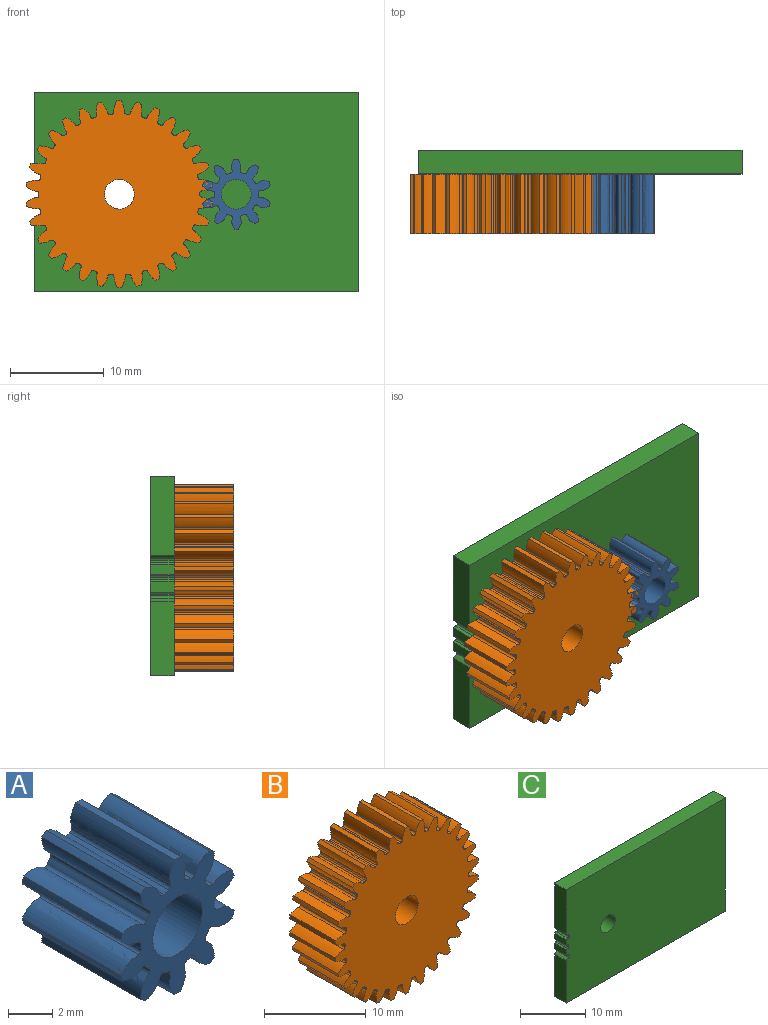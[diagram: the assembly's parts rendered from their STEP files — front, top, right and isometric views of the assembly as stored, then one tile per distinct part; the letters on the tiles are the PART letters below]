
ASSEMBLY  parts=3 mates=2
PART A: 63 faces, bbox 7.3x6.4x7.5 mm
  f0: cylinder r=3.75mm len=6.35mm, axis (0,1,0), area 2.3mm2, adj f9,f12,f53,f60
  f1: cylinder r=3.75mm len=6.35mm, axis (0,1,0), area 2.3mm2, adj f9,f12,f13,f55
  f2: cylinder r=3.75mm len=6.35mm, axis (0,1,0), area 2.3mm2, adj f9,f12,f43,f50
  f3: cylinder r=3.75mm len=6.35mm, axis (0,1,0), area 2.3mm2, adj f9,f12,f45,f58
  f4: cylinder r=3.75mm len=6.35mm, axis (0,1,0), area 2.3mm2, adj f9,f12,f33,f40
  f5: cylinder r=3.75mm len=6.35mm, axis (0,1,0), area 2.3mm2, adj f9,f12,f28,f35
  f6: cylinder r=3.75mm len=6.35mm, axis (0,1,0), area 2.3mm2, adj f9,f12,f23,f30
  f7: cylinder r=3.75mm len=6.35mm, axis (0,1,0), area 2.3mm2, adj f9,f12,f25,f48
  f8: cylinder r=3.75mm len=6.35mm, axis (0,1,0), area 2.3mm2, adj f9,f12,f20,f38
  f9: plane 7.51x7.25mm, normal (0,-1,0), area 21.3mm2, adj f0,f1,f2,f3,f4,f5,f6,f7
  f10: cylinder r=1.59mm len=6.35mm, axis (0,1,0), area 63.3mm2, adj f9,f12
  f11: cylinder r=3.75mm len=6.35mm, axis (0,1,0), area 2.3mm2, adj f9,f12,f15,f18
  f12: plane 7.51x7.25mm, normal (0,1,0), area 21.3mm2, adj f0,f1,f2,f3,f4,f5,f6,f7
  f13: extruded ~6.35x1.11mm, area 8.4mm2, adj f1,f9,f12,f16
  f14: cylinder r=2.34mm len=6.35mm, axis (0,1,0), area 2mm2, adj f9,f12,f16,f17
  f15: extruded ~6.35x1.11mm, area 8.4mm2, adj f9,f11,f12,f17
  f16: cylinder r=0.19mm len=6.35mm, axis (0,1,0), area 1.8mm2, adj f9,f12,f13,f14
  f17: cylinder r=0.19mm len=6.35mm, axis (0,1,0), area 1.8mm2, adj f9,f12,f14,f15
  f18: extruded ~6.35x1.27mm, area 8.4mm2, adj f9,f11,f12,f21
  f19: cylinder r=2.34mm len=6.35mm, axis (0,1,0), area 2mm2, adj f9,f12,f21,f22
  f20: extruded ~6.35x1.16mm, area 8.4mm2, adj f8,f9,f12,f22
  f21: cylinder r=0.19mm len=6.35mm, axis (0,1,0), area 1.8mm2, adj f9,f12,f18,f19
  f22: cylinder r=0.19mm len=6.35mm, axis (0,1,0), area 1.8mm2, adj f9,f12,f19,f20
  f23: extruded ~6.35x1.11mm, area 8.4mm2, adj f6,f9,f12,f26
  f24: cylinder r=2.34mm len=6.35mm, axis (0,1,0), area 2mm2, adj f9,f12,f26,f27
  f25: extruded ~6.35x1.11mm, area 8.4mm2, adj f7,f9,f12,f27
  f26: cylinder r=0.19mm len=6.35mm, axis (0,1,0), area 1.8mm2, adj f9,f12,f23,f24
  f27: cylinder r=0.19mm len=6.35mm, axis (0,1,0), area 1.8mm2, adj f9,f12,f24,f25
  f28: extruded ~6.35x1.16mm, area 8.4mm2, adj f5,f9,f12,f31
  f29: cylinder r=2.34mm len=6.35mm, axis (0,1,0), area 2mm2, adj f9,f12,f31,f32
  f30: extruded ~6.35x1.27mm, area 8.4mm2, adj f6,f9,f12,f32
  f31: cylinder r=0.19mm len=6.35mm, axis (0,1,0), area 1.8mm2, adj f9,f12,f28,f29
  f32: cylinder r=0.19mm len=6.35mm, axis (0,1,0), area 1.8mm2, adj f9,f12,f29,f30
  f33: extruded ~6.35x1.25mm, area 8.4mm2, adj f4,f9,f12,f36
  f34: cylinder r=2.34mm len=6.35mm, axis (0,1,0), area 2mm2, adj f9,f12,f36,f37
  f35: extruded ~6.35x0.94mm, area 8.4mm2, adj f5,f9,f12,f37
  f36: cylinder r=0.19mm len=6.35mm, axis (0,1,0), area 1.8mm2, adj f9,f12,f33,f34
  f37: cylinder r=0.19mm len=6.35mm, axis (0,1,0), area 1.8mm2, adj f9,f12,f34,f35
  f38: extruded ~6.35x0.94mm, area 8.4mm2, adj f8,f9,f12,f41
  f39: cylinder r=2.34mm len=6.35mm, axis (0,1,0), area 2mm2, adj f9,f12,f41,f42
  f40: extruded ~6.35x1.25mm, area 8.4mm2, adj f4,f9,f12,f42
  f41: cylinder r=0.19mm len=6.35mm, axis (0,1,0), area 1.8mm2, adj f9,f12,f38,f39
  f42: cylinder r=0.19mm len=6.35mm, axis (0,1,0), area 1.8mm2, adj f9,f12,f39,f40
  f43: extruded ~6.35x0.94mm, area 8.4mm2, adj f2,f9,f12,f46
  f44: cylinder r=2.34mm len=6.35mm, axis (0,1,0), area 2mm2, adj f9,f12,f46,f47
  f45: extruded ~6.35x1.25mm, area 8.4mm2, adj f3,f9,f12,f47
  f46: cylinder r=0.19mm len=6.35mm, axis (0,1,0), area 1.8mm2, adj f9,f12,f43,f44
  f47: cylinder r=0.19mm len=6.35mm, axis (0,1,0), area 1.8mm2, adj f9,f12,f44,f45
  f48: extruded ~6.35x1.27mm, area 8.4mm2, adj f7,f9,f12,f51
  f49: cylinder r=2.34mm len=6.35mm, axis (0,1,0), area 2mm2, adj f9,f12,f51,f52
  f50: extruded ~6.35x1.16mm, area 8.4mm2, adj f2,f9,f12,f52
  f51: cylinder r=0.19mm len=6.35mm, axis (0,1,0), area 1.8mm2, adj f9,f12,f48,f49
  f52: cylinder r=0.19mm len=6.35mm, axis (0,1,0), area 1.8mm2, adj f9,f12,f49,f50
  f53: extruded ~6.35x1.16mm, area 8.4mm2, adj f0,f9,f12,f56
  f54: cylinder r=2.34mm len=6.35mm, axis (0,1,0), area 2mm2, adj f9,f12,f56,f57
  f55: extruded ~6.35x1.27mm, area 8.4mm2, adj f1,f9,f12,f57
  f56: cylinder r=0.19mm len=6.35mm, axis (0,1,0), area 1.8mm2, adj f9,f12,f53,f54
  f57: cylinder r=0.19mm len=6.35mm, axis (0,1,0), area 1.8mm2, adj f9,f12,f54,f55
  f58: extruded ~6.35x1.25mm, area 8.4mm2, adj f3,f9,f12,f61
  f59: cylinder r=2.34mm len=6.35mm, axis (0,1,0), area 2mm2, adj f9,f12,f61,f62
  f60: extruded ~6.35x0.94mm, area 8.4mm2, adj f0,f9,f12,f62
  f61: cylinder r=0.19mm len=6.35mm, axis (0,1,0), area 1.8mm2, adj f9,f12,f58,f59
  f62: cylinder r=0.19mm len=6.35mm, axis (0,1,0), area 1.8mm2, adj f9,f12,f59,f60
PART B: 183 faces, bbox 19.9x6.4x20 mm
  f0: cylinder r=10mm len=6.35mm, axis (0,1,0), area 2.9mm2, adj f29,f32,f173,f180
  f1: cylinder r=10mm len=6.35mm, axis (0,1,0), area 2.9mm2, adj f29,f32,f168,f175
  f2: cylinder r=10mm len=6.35mm, axis (0,1,0), area 2.9mm2, adj f29,f32,f163,f170
  f3: cylinder r=10mm len=6.35mm, axis (0,1,0), area 2.9mm2, adj f29,f32,f153,f165
  f4: cylinder r=10mm len=6.35mm, axis (0,1,0), area 2.9mm2, adj f29,f32,f148,f160
  f5: cylinder r=10mm len=6.35mm, axis (0,1,0), area 2.9mm2, adj f29,f32,f155,f158
  f6: cylinder r=10mm len=6.35mm, axis (0,1,0), area 2.9mm2, adj f29,f32,f143,f150
  f7: cylinder r=10mm len=6.35mm, axis (0,1,0), area 2.9mm2, adj f29,f32,f33,f145
  f8: cylinder r=10mm len=6.35mm, axis (0,1,0), area 2.9mm2, adj f29,f32,f128,f140
  f9: cylinder r=10mm len=6.35mm, axis (0,1,0), area 2.9mm2, adj f29,f32,f135,f138
  f10: cylinder r=10mm len=6.35mm, axis (0,1,0), area 2.9mm2, adj f29,f32,f123,f130
  f11: cylinder r=10mm len=6.35mm, axis (0,1,0), area 2.9mm2, adj f29,f32,f125,f178
  f12: cylinder r=10mm len=6.35mm, axis (0,1,0), area 2.9mm2, adj f29,f32,f120,f133
  f13: cylinder r=10mm len=6.35mm, axis (0,1,0), area 2.9mm2, adj f29,f32,f115,f118
  f14: cylinder r=10mm len=6.35mm, axis (0,1,0), area 2.9mm2, adj f29,f32,f110,f113
  f15: cylinder r=10mm len=6.35mm, axis (0,1,0), area 2.9mm2, adj f29,f32,f105,f108
  f16: cylinder r=10mm len=6.35mm, axis (0,1,0), area 2.9mm2, adj f29,f32,f88,f100
  f17: cylinder r=10mm len=6.35mm, axis (0,1,0), area 2.9mm2, adj f29,f32,f95,f98
  f18: cylinder r=10mm len=6.35mm, axis (0,1,0), area 2.9mm2, adj f29,f32,f83,f90
  f19: cylinder r=10mm len=6.35mm, axis (0,1,0), area 2.9mm2, adj f29,f32,f85,f103
  f20: cylinder r=10mm len=6.35mm, axis (0,1,0), area 2.9mm2, adj f29,f32,f80,f93
  f21: cylinder r=10mm len=6.35mm, axis (0,1,0), area 2.9mm2, adj f29,f32,f75,f78
  f22: cylinder r=10mm len=6.35mm, axis (0,1,0), area 2.9mm2, adj f29,f32,f70,f73
  f23: cylinder r=10mm len=6.35mm, axis (0,1,0), area 2.9mm2, adj f29,f32,f65,f68
  f24: cylinder r=10mm len=6.35mm, axis (0,1,0), area 2.9mm2, adj f29,f32,f53,f60
  f25: cylinder r=10mm len=6.35mm, axis (0,1,0), area 2.9mm2, adj f29,f32,f43,f55
  f26: cylinder r=10mm len=6.35mm, axis (0,1,0), area 2.9mm2, adj f29,f32,f50,f63
  f27: cylinder r=10mm len=6.35mm, axis (0,1,0), area 2.9mm2, adj f29,f32,f45,f48
  f28: cylinder r=10mm len=6.35mm, axis (0,1,0), area 2.9mm2, adj f29,f32,f40,f58
  f29: plane 20x19.93mm, normal (0,-1,0), area 265.1mm2, adj f0,f1,f2,f3,f4,f5,f6,f7
  f30: cylinder r=1.59mm len=6.35mm, axis (0,1,0), area 63.3mm2, adj f29,f32
  f31: cylinder r=10mm len=6.35mm, axis (0,1,0), area 2.9mm2, adj f29,f32,f35,f38
  f32: plane 20x19.93mm, normal (0,1,0), area 265.1mm2, adj f0,f1,f2,f3,f4,f5,f6,f7
  f33: extruded ~6.35x1.16mm, area 8mm2, adj f7,f29,f32,f36
  f34: cylinder r=8.59mm len=6.35mm, axis (0,1,0), area 1.2mm2, adj f29,f32,f36,f37
  f35: extruded ~6.35x1.16mm, area 8mm2, adj f29,f31,f32,f37
  f36: cylinder r=0.23mm len=6.35mm, axis (0,1,0), area 2.2mm2, adj f29,f32,f33,f34
  f37: cylinder r=0.23mm len=6.35mm, axis (0,1,0), area 2.2mm2, adj f29,f32,f34,f35
  f38: extruded ~6.35x1.23mm, area 8mm2, adj f29,f31,f32,f41
  f39: cylinder r=8.59mm len=6.35mm, axis (0,1,0), area 1.2mm2, adj f29,f32,f41,f42
  f40: extruded ~6.35x1.03mm, area 8mm2, adj f28,f29,f32,f42
  f41: cylinder r=0.23mm len=6.35mm, axis (0,1,0), area 2.2mm2, adj f29,f32,f38,f39
  f42: cylinder r=0.23mm len=6.35mm, axis (0,1,0), area 2.2mm2, adj f29,f32,f39,f40
  f43: extruded ~6.35x1.14mm, area 8mm2, adj f25,f29,f32,f46
  f44: cylinder r=8.59mm len=6.35mm, axis (0,1,0), area 1.2mm2, adj f29,f32,f46,f47
  f45: extruded ~6.35x1.19mm, area 8mm2, adj f27,f29,f32,f47
  f46: cylinder r=0.23mm len=6.35mm, axis (0,1,0), area 2.2mm2, adj f29,f32,f43,f44
  f47: cylinder r=0.23mm len=6.35mm, axis (0,1,0), area 2.2mm2, adj f29,f32,f44,f45
  f48: extruded ~6.35x1mm, area 8mm2, adj f27,f29,f32,f51
  f49: cylinder r=8.59mm len=6.35mm, axis (0,1,0), area 1.2mm2, adj f29,f32,f51,f52
  f50: extruded ~6.35x1.25mm, area 8mm2, adj f26,f29,f32,f52
  f51: cylinder r=0.23mm len=6.35mm, axis (0,1,0), area 2.2mm2, adj f29,f32,f48,f49
  f52: cylinder r=0.23mm len=6.35mm, axis (0,1,0), area 2.2mm2, adj f29,f32,f49,f50
  f53: extruded ~6.35x1.22mm, area 8mm2, adj f24,f29,f32,f56
  f54: cylinder r=8.59mm len=6.35mm, axis (0,1,0), area 1.2mm2, adj f29,f32,f56,f57
  f55: extruded ~6.35x1.07mm, area 8mm2, adj f25,f29,f32,f57
  f56: cylinder r=0.23mm len=6.35mm, axis (0,1,0), area 2.2mm2, adj f29,f32,f53,f54
  f57: cylinder r=0.23mm len=6.35mm, axis (0,1,0), area 2.2mm2, adj f29,f32,f54,f55
  f58: extruded ~6.35x1.26mm, area 8mm2, adj f28,f29,f32,f61
  f59: cylinder r=8.59mm len=6.35mm, axis (0,1,0), area 1.2mm2, adj f29,f32,f61,f62
  f60: extruded ~6.35x0.92mm, area 8mm2, adj f24,f29,f32,f62
  f61: cylinder r=0.23mm len=6.35mm, axis (0,1,0), area 2.2mm2, adj f29,f32,f58,f59
  f62: cylinder r=0.23mm len=6.35mm, axis (0,1,0), area 2.2mm2, adj f29,f32,f59,f60
  f63: extruded ~6.35x0.95mm, area 8mm2, adj f26,f29,f32,f66
  f64: cylinder r=8.59mm len=6.35mm, axis (0,1,0), area 1.2mm2, adj f29,f32,f66,f67
  f65: extruded ~6.35x1.25mm, area 8mm2, adj f23,f29,f32,f67
  f66: cylinder r=0.23mm len=6.35mm, axis (0,1,0), area 2.2mm2, adj f29,f32,f63,f64
  f67: cylinder r=0.23mm len=6.35mm, axis (0,1,0), area 2.2mm2, adj f29,f32,f64,f65
  f68: extruded ~6.35x1.1mm, area 8mm2, adj f23,f29,f32,f71
  f69: cylinder r=8.59mm len=6.35mm, axis (0,1,0), area 1.2mm2, adj f29,f32,f71,f72
  f70: extruded ~6.35x1.2mm, area 8mm2, adj f22,f29,f32,f72
  f71: cylinder r=0.23mm len=6.35mm, axis (0,1,0), area 2.2mm2, adj f29,f32,f68,f69
  f72: cylinder r=0.23mm len=6.35mm, axis (0,1,0), area 2.2mm2, adj f29,f32,f69,f70
  f73: extruded ~6.35x1.2mm, area 8mm2, adj f22,f29,f32,f76
  f74: cylinder r=8.59mm len=6.35mm, axis (0,1,0), area 1.2mm2, adj f29,f32,f76,f77
  f75: extruded ~6.35x1.1mm, area 8mm2, adj f21,f29,f32,f77
  f76: cylinder r=0.23mm len=6.35mm, axis (0,1,0), area 2.2mm2, adj f29,f32,f73,f74
  f77: cylinder r=0.23mm len=6.35mm, axis (0,1,0), area 2.2mm2, adj f29,f32,f74,f75
  f78: extruded ~6.35x1.25mm, area 8mm2, adj f21,f29,f32,f81
  f79: cylinder r=8.59mm len=6.35mm, axis (0,1,0), area 1.2mm2, adj f29,f32,f81,f82
  f80: extruded ~6.35x0.95mm, area 8mm2, adj f20,f29,f32,f82
  f81: cylinder r=0.23mm len=6.35mm, axis (0,1,0), area 2.2mm2, adj f29,f32,f78,f79
  f82: cylinder r=0.23mm len=6.35mm, axis (0,1,0), area 2.2mm2, adj f29,f32,f79,f80
  f83: extruded ~6.35x0.92mm, area 8mm2, adj f18,f29,f32,f86
  f84: cylinder r=8.59mm len=6.35mm, axis (0,1,0), area 1.2mm2, adj f29,f32,f86,f87
  f85: extruded ~6.35x1.26mm, area 8mm2, adj f19,f29,f32,f87
  f86: cylinder r=0.23mm len=6.35mm, axis (0,1,0), area 2.2mm2, adj f29,f32,f83,f84
  f87: cylinder r=0.23mm len=6.35mm, axis (0,1,0), area 2.2mm2, adj f29,f32,f84,f85
  f88: extruded ~6.35x1.07mm, area 8mm2, adj f16,f29,f32,f91
  f89: cylinder r=8.59mm len=6.35mm, axis (0,1,0), area 1.2mm2, adj f29,f32,f91,f92
  f90: extruded ~6.35x1.22mm, area 8mm2, adj f18,f29,f32,f92
  f91: cylinder r=0.23mm len=6.35mm, axis (0,1,0), area 2.2mm2, adj f29,f32,f88,f89
  f92: cylinder r=0.23mm len=6.35mm, axis (0,1,0), area 2.2mm2, adj f29,f32,f89,f90
  f93: extruded ~6.35x1.25mm, area 8mm2, adj f20,f29,f32,f96
  f94: cylinder r=8.59mm len=6.35mm, axis (0,1,0), area 1.2mm2, adj f29,f32,f96,f97
  f95: extruded ~6.35x1mm, area 8mm2, adj f17,f29,f32,f97
  f96: cylinder r=0.23mm len=6.35mm, axis (0,1,0), area 2.2mm2, adj f29,f32,f93,f94
  f97: cylinder r=0.23mm len=6.35mm, axis (0,1,0), area 2.2mm2, adj f29,f32,f94,f95
  f98: extruded ~6.35x1.19mm, area 8mm2, adj f17,f29,f32,f101
  f99: cylinder r=8.59mm len=6.35mm, axis (0,1,0), area 1.2mm2, adj f29,f32,f101,f102
  f100: extruded ~6.35x1.14mm, area 8mm2, adj f16,f29,f32,f102
  f101: cylinder r=0.23mm len=6.35mm, axis (0,1,0), area 2.2mm2, adj f29,f32,f98,f99
  f102: cylinder r=0.23mm len=6.35mm, axis (0,1,0), area 2.2mm2, adj f29,f32,f99,f100
  f103: extruded ~6.35x1.03mm, area 8mm2, adj f19,f29,f32,f106
  f104: cylinder r=8.59mm len=6.35mm, axis (0,1,0), area 1.2mm2, adj f29,f32,f106,f107
  f105: extruded ~6.35x1.23mm, area 8mm2, adj f15,f29,f32,f107
  f106: cylinder r=0.23mm len=6.35mm, axis (0,1,0), area 2.2mm2, adj f29,f32,f103,f104
  f107: cylinder r=0.23mm len=6.35mm, axis (0,1,0), area 2.2mm2, adj f29,f32,f104,f105
  f108: extruded ~6.35x1.16mm, area 8mm2, adj f15,f29,f32,f111
  f109: cylinder r=8.59mm len=6.35mm, axis (0,1,0), area 1.2mm2, adj f29,f32,f111,f112
  f110: extruded ~6.35x1.16mm, area 8mm2, adj f14,f29,f32,f112
  f111: cylinder r=0.23mm len=6.35mm, axis (0,1,0), area 2.2mm2, adj f29,f32,f108,f109
  f112: cylinder r=0.23mm len=6.35mm, axis (0,1,0), area 2.2mm2, adj f29,f32,f109,f110
  f113: extruded ~6.35x1.23mm, area 8mm2, adj f14,f29,f32,f116
  f114: cylinder r=8.59mm len=6.35mm, axis (0,1,0), area 1.2mm2, adj f29,f32,f116,f117
  f115: extruded ~6.35x1.03mm, area 8mm2, adj f13,f29,f32,f117
  f116: cylinder r=0.23mm len=6.35mm, axis (0,1,0), area 2.2mm2, adj f29,f32,f113,f114
  f117: cylinder r=0.23mm len=6.35mm, axis (0,1,0), area 2.2mm2, adj f29,f32,f114,f115
  f118: extruded ~6.35x1.26mm, area 8mm2, adj f13,f29,f32,f121
  f119: cylinder r=8.59mm len=6.35mm, axis (0,1,0), area 1.2mm2, adj f29,f32,f121,f122
  f120: extruded ~6.35x0.92mm, area 8mm2, adj f12,f29,f32,f122
  f121: cylinder r=0.23mm len=6.35mm, axis (0,1,0), area 2.2mm2, adj f29,f32,f118,f119
  f122: cylinder r=0.23mm len=6.35mm, axis (0,1,0), area 2.2mm2, adj f29,f32,f119,f120
  f123: extruded ~6.35x0.95mm, area 8mm2, adj f10,f29,f32,f126
  f124: cylinder r=8.59mm len=6.35mm, axis (0,1,0), area 1.2mm2, adj f29,f32,f126,f127
  f125: extruded ~6.35x1.25mm, area 8mm2, adj f11,f29,f32,f127
  f126: cylinder r=0.23mm len=6.35mm, axis (0,1,0), area 2.2mm2, adj f29,f32,f123,f124
  f127: cylinder r=0.23mm len=6.35mm, axis (0,1,0), area 2.2mm2, adj f29,f32,f124,f125
  f128: extruded ~6.35x1mm, area 8mm2, adj f8,f29,f32,f131
  f129: cylinder r=8.59mm len=6.35mm, axis (0,1,0), area 1.2mm2, adj f29,f32,f131,f132
  f130: extruded ~6.35x1.25mm, area 8mm2, adj f10,f29,f32,f132
  f131: cylinder r=0.23mm len=6.35mm, axis (0,1,0), area 2.2mm2, adj f29,f32,f128,f129
  f132: cylinder r=0.23mm len=6.35mm, axis (0,1,0), area 2.2mm2, adj f29,f32,f129,f130
  f133: extruded ~6.35x1.22mm, area 8mm2, adj f12,f29,f32,f136
  f134: cylinder r=8.59mm len=6.35mm, axis (0,1,0), area 1.2mm2, adj f29,f32,f136,f137
  f135: extruded ~6.35x1.07mm, area 8mm2, adj f9,f29,f32,f137
  f136: cylinder r=0.23mm len=6.35mm, axis (0,1,0), area 2.2mm2, adj f29,f32,f133,f134
  f137: cylinder r=0.23mm len=6.35mm, axis (0,1,0), area 2.2mm2, adj f29,f32,f134,f135
  f138: extruded ~6.35x1.14mm, area 8mm2, adj f9,f29,f32,f141
  f139: cylinder r=8.59mm len=6.35mm, axis (0,1,0), area 1.2mm2, adj f29,f32,f141,f142
  f140: extruded ~6.35x1.19mm, area 8mm2, adj f8,f29,f32,f142
  f141: cylinder r=0.23mm len=6.35mm, axis (0,1,0), area 2.2mm2, adj f29,f32,f138,f139
  f142: cylinder r=0.23mm len=6.35mm, axis (0,1,0), area 2.2mm2, adj f29,f32,f139,f140
  f143: extruded ~6.35x1.03mm, area 8mm2, adj f6,f29,f32,f146
  f144: cylinder r=8.59mm len=6.35mm, axis (0,1,0), area 1.2mm2, adj f29,f32,f146,f147
  f145: extruded ~6.35x1.23mm, area 8mm2, adj f7,f29,f32,f147
  f146: cylinder r=0.23mm len=6.35mm, axis (0,1,0), area 2.2mm2, adj f29,f32,f143,f144
  f147: cylinder r=0.23mm len=6.35mm, axis (0,1,0), area 2.2mm2, adj f29,f32,f144,f145
  f148: extruded ~6.35x0.92mm, area 8mm2, adj f4,f29,f32,f151
  f149: cylinder r=8.59mm len=6.35mm, axis (0,1,0), area 1.2mm2, adj f29,f32,f151,f152
  f150: extruded ~6.35x1.26mm, area 8mm2, adj f6,f29,f32,f152
  f151: cylinder r=0.23mm len=6.35mm, axis (0,1,0), area 2.2mm2, adj f29,f32,f148,f149
  f152: cylinder r=0.23mm len=6.35mm, axis (0,1,0), area 2.2mm2, adj f29,f32,f149,f150
  f153: extruded ~6.35x1.19mm, area 8mm2, adj f3,f29,f32,f156
  f154: cylinder r=8.59mm len=6.35mm, axis (0,1,0), area 1.2mm2, adj f29,f32,f156,f157
  f155: extruded ~6.35x1.14mm, area 8mm2, adj f5,f29,f32,f157
  f156: cylinder r=0.23mm len=6.35mm, axis (0,1,0), area 2.2mm2, adj f29,f32,f153,f154
  f157: cylinder r=0.23mm len=6.35mm, axis (0,1,0), area 2.2mm2, adj f29,f32,f154,f155
  f158: extruded ~6.35x1.07mm, area 8mm2, adj f5,f29,f32,f161
  f159: cylinder r=8.59mm len=6.35mm, axis (0,1,0), area 1.2mm2, adj f29,f32,f161,f162
  f160: extruded ~6.35x1.22mm, area 8mm2, adj f4,f29,f32,f162
  f161: cylinder r=0.23mm len=6.35mm, axis (0,1,0), area 2.2mm2, adj f29,f32,f158,f159
  f162: cylinder r=0.23mm len=6.35mm, axis (0,1,0), area 2.2mm2, adj f29,f32,f159,f160
  f163: extruded ~6.35x1.25mm, area 8mm2, adj f2,f29,f32,f166
  f164: cylinder r=8.59mm len=6.35mm, axis (0,1,0), area 1.2mm2, adj f29,f32,f166,f167
  f165: extruded ~6.35x1mm, area 8mm2, adj f3,f29,f32,f167
  f166: cylinder r=0.23mm len=6.35mm, axis (0,1,0), area 2.2mm2, adj f29,f32,f163,f164
  f167: cylinder r=0.23mm len=6.35mm, axis (0,1,0), area 2.2mm2, adj f29,f32,f164,f165
  f168: extruded ~6.35x1.25mm, area 8mm2, adj f1,f29,f32,f171
  f169: cylinder r=8.59mm len=6.35mm, axis (0,1,0), area 1.2mm2, adj f29,f32,f171,f172
  f170: extruded ~6.35x0.95mm, area 8mm2, adj f2,f29,f32,f172
  f171: cylinder r=0.23mm len=6.35mm, axis (0,1,0), area 2.2mm2, adj f29,f32,f168,f169
  f172: cylinder r=0.23mm len=6.35mm, axis (0,1,0), area 2.2mm2, adj f29,f32,f169,f170
  f173: extruded ~6.35x1.2mm, area 8mm2, adj f0,f29,f32,f176
  f174: cylinder r=8.59mm len=6.35mm, axis (0,1,0), area 1.2mm2, adj f29,f32,f176,f177
  f175: extruded ~6.35x1.1mm, area 8mm2, adj f1,f29,f32,f177
  f176: cylinder r=0.23mm len=6.35mm, axis (0,1,0), area 2.2mm2, adj f29,f32,f173,f174
  f177: cylinder r=0.23mm len=6.35mm, axis (0,1,0), area 2.2mm2, adj f29,f32,f174,f175
  f178: extruded ~6.35x1.1mm, area 8mm2, adj f11,f29,f32,f181
  f179: cylinder r=8.59mm len=6.35mm, axis (0,1,0), area 1.2mm2, adj f29,f32,f181,f182
  f180: extruded ~6.35x1.2mm, area 8mm2, adj f0,f29,f32,f182
  f181: cylinder r=0.23mm len=6.35mm, axis (0,1,0), area 2.2mm2, adj f29,f32,f178,f179
  f182: cylinder r=0.23mm len=6.35mm, axis (0,1,0), area 2.2mm2, adj f29,f32,f179,f180
PART C: 25 faces, bbox 34.6x2.5x21.3 mm
  f0: plane 7.95x2.54mm, normal (-1,0,0), area 20.2mm2, adj f1,f21,f23,f24
  f1: extruded ~2.54x0.56mm, area 1.6mm2, adj f0,f2,f23,f24
  f2: cylinder r=0.23mm len=2.54mm, axis (0,-1,0), area 0.9mm2, adj f1,f3,f23,f24
  f3: cylinder r=8.59mm len=2.54mm, axis (0,-1,0), area 0.5mm2, adj f2,f4,f23,f24
  f4: cylinder r=0.23mm len=2.54mm, axis (0,-1,0), area 0.9mm2, adj f3,f5,f23,f24
  f5: extruded ~2.54x0.43mm, area 1.1mm2, adj f4,f6,f23,f24
  f6: plane 2.54x1.1mm, normal (-1,0,0), area 2.8mm2, adj f5,f7,f23,f24
  f7: extruded ~2.54x0.3mm, area 0.8mm2, adj f6,f8,f23,f24
  f8: cylinder r=0.23mm len=2.54mm, axis (0,-1,0), area 0.9mm2, adj f7,f9,f23,f24
  f9: cylinder r=8.59mm len=2.54mm, axis (0,-1,0), area 0.5mm2, adj f8,f10,f23,f24
  f10: cylinder r=0.23mm len=2.54mm, axis (0,-1,0), area 0.9mm2, adj f9,f11,f23,f24
  f11: extruded ~2.54x0.3mm, area 0.8mm2, adj f10,f12,f23,f24
  f12: plane 2.54x1.1mm, normal (-1,0,0), area 2.8mm2, adj f11,f13,f23,f24
  f13: extruded ~2.54x0.43mm, area 1.1mm2, adj f12,f14,f23,f24
  f14: cylinder r=0.23mm len=2.54mm, axis (0,-1,0), area 0.9mm2, adj f13,f15,f23,f24
  f15: cylinder r=8.59mm len=2.54mm, axis (0,-1,0), area 0.5mm2, adj f14,f16,f23,f24
  f16: cylinder r=0.23mm len=2.54mm, axis (0,-1,0), area 0.9mm2, adj f15,f17,f23,f24
  f17: extruded ~2.54x0.56mm, area 1.6mm2, adj f16,f18,f23,f24
  f18: plane 8.44x2.54mm, normal (-1,0,0), area 21.4mm2, adj f17,f19,f23,f24
  f19: plane 34.61x2.54mm, normal (0,0,1), area 87.9mm2, adj f18,f20,f23,f24
  f20: plane 21.33x2.54mm, normal (1,0,0), area 54.2mm2, adj f19,f21,f23,f24
  f21: plane 34.61x2.54mm, normal (0,0,-1), area 87.9mm2, adj f0,f20,f23,f24
  f22: cylinder r=1.59mm len=3.18mm, axis (0,-1,0), area 25.3mm2, adj f23,f24
  f23: plane 34.61x21.33mm, normal (0,1,0), area 728.9mm2, adj f0,f1,f2,f3,f4,f5,f6,f7
  f24: plane 34.61x21.33mm, normal (0,-1,0), area 728.9mm2, adj f0,f1,f2,f3,f4,f5,f6,f7
PLACE A rot(axis=(0,-1,0),144.5deg) t=(57.03,-38.06,14.98)mm
PLACE B rot(axis=(0,1,0),71.8deg) t=(34.36,-38.06,22.24)mm
PLACE C t=(34.36,-38.06,22.24)mm fixed
MATE revolute C.f24 <-> A.f0  axis (0,-1,0) through (46.86,-38.06,22.24)mm
MATE revolute C.f3 <-> B.f0  axis (0,-1,0) through (34.36,-38.06,22.24)mm
